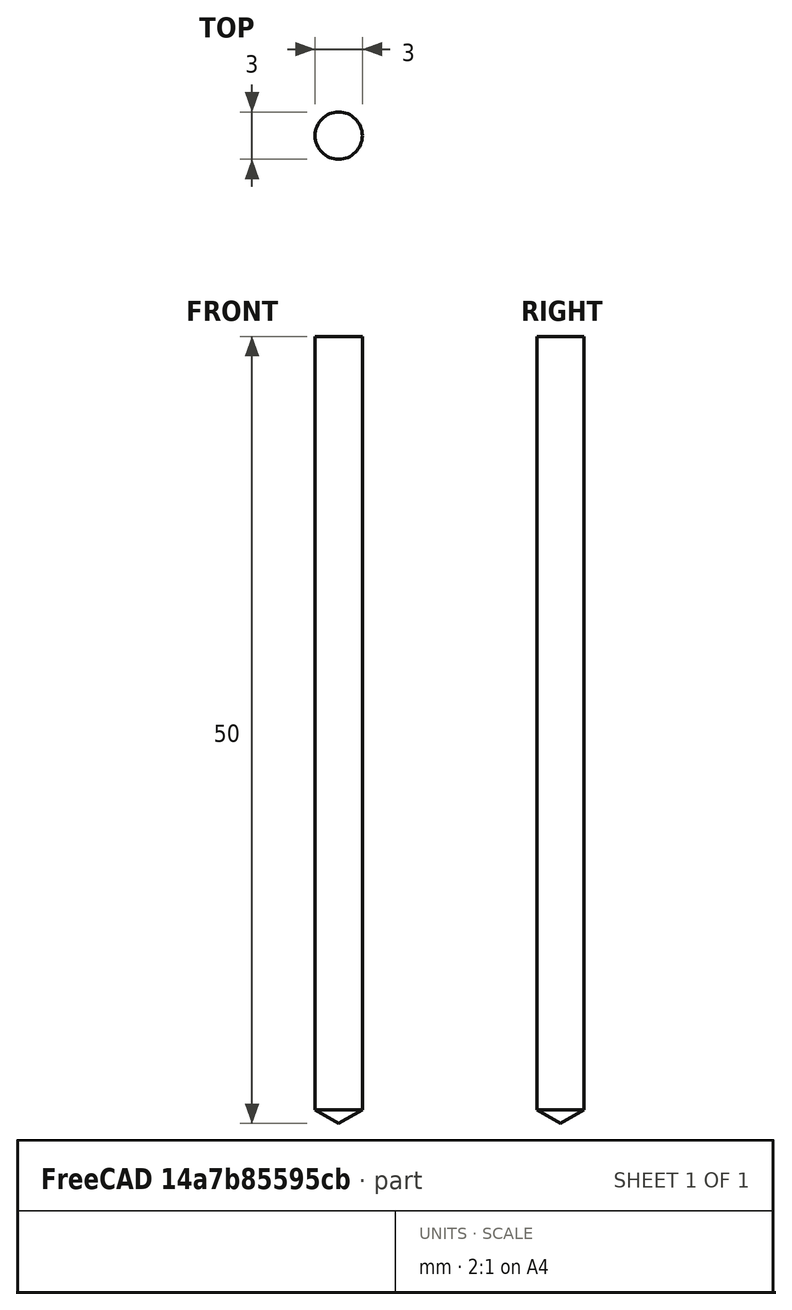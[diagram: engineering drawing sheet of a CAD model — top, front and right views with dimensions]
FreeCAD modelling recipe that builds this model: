
FCSTD DOCUMENT  (FreeCAD 1.0R39109 (Git))
Label: drill
License: Creative Commons Attribution 4.0
LicenseURL: https://creativecommons.org/licenses/by/4.0/
objects: Sketcher::SketchObject×1, PartDesign::Revolution×1, App::FeaturePython×1, PartDesign::Body×1
note: 6 computed .brp shape members not serialized (recipe doc carries the construction recipe); baked Part::Feature solids carry a one-line shape summary decoded from their .brp

FEATURE [Sketcher::SketchObject] Sketch
  ArcFitTolerance = 0
  AttachmentSupport = -> [XZ_Plane]
  FullyConstrained = true
  MakeInternals = false
  MapMode = 5
  Placement = pos=(0,0,0) rot=(1,0,0;1.5708rad)
  expr: Constraints[13] = <<Attributes>>.TipAngle
  expr: Constraints[14] = <<Attributes>>.Diameter
  expr: Constraints[15] = <<Attributes>>.Length
  sketch-geometry (7):
    g0: LineSegment StartX=0 StartY=50 StartZ=0 EndX=0 EndY=0 EndZ=0
    g1: LineSegment StartX=0 StartY=0 StartZ=0 EndX=1.5 EndY=0.883568 EndZ=0
    g2: LineSegment StartX=1.5 StartY=0.883568 StartZ=0 EndX=1.5 EndY=50 EndZ=0
    g3: LineSegment StartX=1.5 StartY=50 StartZ=0 EndX=0 EndY=50 EndZ=0
    g4: LineSegment [constr] StartX=1.5 StartY=0.883568 StartZ=0 EndX=-1.5 EndY=0.883568 EndZ=0
    g5: LineSegment [constr] StartX=-1.5 StartY=0.883568 StartZ=0 EndX=0 EndY=0 EndZ=0
    g6: LineSegment [constr] StartX=0 StartY=0 StartZ=0 EndX=1.5 EndY=0.883568 EndZ=0
  constraints (17):
    c: Vertical(g0)
    c: Coincident(g0,g1)
    c: Coincident(g1,g2)
    c: Vertical(g2)
    c: Coincident(g2,g3)
    c: Horizontal(g3)
    c: Coincident(g0,g3)
    c: Coincident(g4,g5)
    c: Coincident(g5,g6)
    c: Coincident(g6,g4)
    c: Coincident(g1,g4)
    c: Coincident(g5,g0)
    c: Symmetric(g4,g1,g0)
    c: Angle(g1,g5) = 2.07694
    c: DistanceX(g4,g4) = 3
    c: DistanceY(g0,g0) = 50
    c: Coincident(g0,g-1)
FEATURE [PartDesign::Revolution] Revolution
  AllowMultiFace = false
  Angle = 360
  Angle2 = 60
  Axis = (0,2e-16,1)
  Base = (0,0,0)
  Placement = pos=(0,0,0) rot=(1,0,0;1.5708rad)
  Profile = -> Sketch
  ReferenceAxis = -> Sketch [V_Axis]
  Reversed = true
  Suppressed = false
  Type = 0
FEATURE [App::FeaturePython] PropertyBag  label="Attributes"  # WARN: FeaturePython — macro-defined, semantics opaque (R4)
  CustomPropertyGroups = 0
  Diameter = 3
  Flutes = 2
  Length = 50
  TipAngle = 119
FEATURE [PartDesign::Body] Body  label="Drill"
  AllowCompound = false
  Group = -> [Sketch,Revolution,PropertyBag]
  Origin = -> Origin
  Tip = -> Revolution
